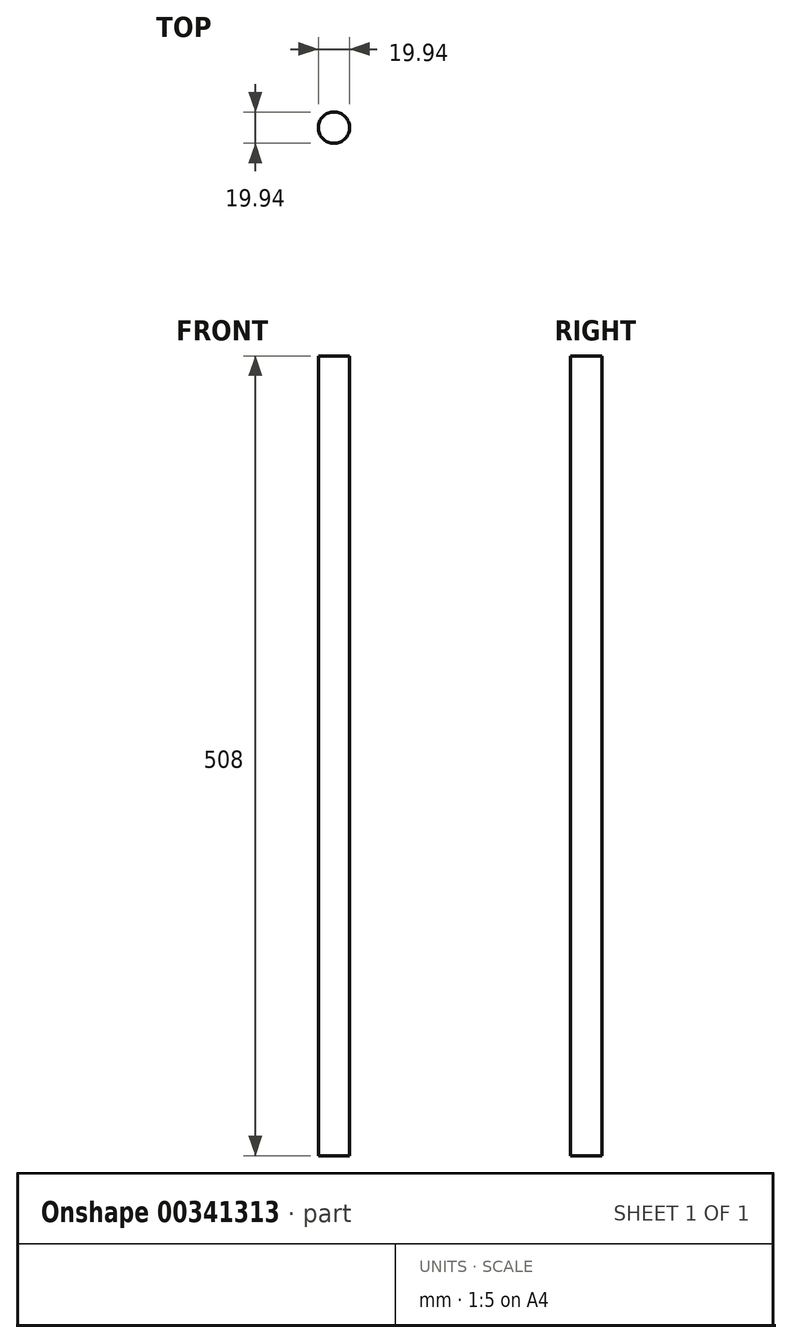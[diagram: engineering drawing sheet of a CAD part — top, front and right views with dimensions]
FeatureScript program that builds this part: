
annotation { "Feature Type Name" : "Feature", "Feature Type Description" : "" }
export const myFeature = defineFeature(function(context is Context, id is Id, definition is map)
    precondition{}
    {
        {
            var Q0;
            Q0=qCreatedBy(makeId("Top.planeOp"),FACE);
            var sketch = newSketch(context, id + "F0", { "sketchPlane" : qUnion([Q0])});
            skCircle(sketch, "E0", {"center": v(0, 0) * mm, "radius": 9.97 * mm});
            skSolve(sketch);
        }
        {
            var Q0;
            Q0 = qSketchRegion(id + "F0", true);
            extrude(context, id + "F1", {"entities" : qUnion([Q0]), "oppositeDirection" : true, "depth" : 508 * mm});
        }
    });
